# Revit family: Spot 1.0
name_source: partatom
category: Lighting Fixtures
revit_build: Autodesk Revit 2017 (Build: 20170419_0315(x64)
units: mm (PartAtom-declared; Revit-internal decimal feet)

## family parameters
Always vertical = No
Cut with Voids When Loaded = No
Light Source = No
OmniClass Number = 23.80.70.00
OmniClass Title = Lighting
Part Type = Normal
Room Calculation Point = No
Round Connector Dimension = Use Diameter
Shared = No
Work Plane-Based = No

## types (5) — shared parameters
Apparent Load Phase 1 = 2 W
Base = L&L_Steel inox AISI 316L
Base bracket = Spot 1.0_Base braket
Body = L&L_Steel inox AISI 316L
Bracket = L&L_Steel inox AISI 316L
CRI = ≥80
Code = -
Control system = -
Cutout dimensions = -
Delivered lumen output = 88 lm (3000K, 500mA, 20°)
Description = projector for outdoor applications (not suitable for use in swimming pools or fountains)
Energy efficiency class = A A+ A++
Features = -
Geometry = Spot 1.0_mod
H1 = 40 mm
Height mm = 55 mm
IP = IP68
LED Colour = 3000K (also available: 2700, 4000K, 5000K, Blue - ref. URL Technical sheet)
Length mm = 57 mm  [stored 0.187008 ft]
Lens = L&L_Tempered extra-clear glass
Lumen output at source = 145 lm (3000K, 500mA)
Manufacturer = L&L Luce&Light
Material = body and trim in AISI 316L stainless steel, screen in transparent, tempered glass
Model = Spot 1.0
Mounting = surface mounted (ceiling, wall, ground, spike, fastener strap)
No. and type of led = 1 power LED, 1/4 ANSI BIN, 50 000h L90 B10 (Ta 25°C)
Notes = version with elliptical optics available on request
Power = 2W
Power cables = includes 1,5 m neoprene cable, H05RN-F 2x0,35/0,75 Ø6,3 mm
Power supply = max 500mA
Power supply unit = not included
not included
not included
URL = https://www.lucelight.it
URL Accessories and power supply units = https://www.lucelight.it
URL Catalogue = https://www.lucelight.it
URL DXF = https://www.lucelight.it
URL Description = https://www.lucelight.it
URL General code = https://www.lucelight.it
URL IES Photometric file = https://www.lucelight.it
URL Image = https://www.lucelight.it
URL Technical sheet = https://www.lucelight.it
Vertical rotation max = 220.00°
Weight kg = 0.40 kg
Width mm = 30 mm  [stored 0.0984252 ft]
Wiring = series
X1 = 100 mm  [stored 0.328084 ft]

## per-type parameters (varying)
| type | Light Source | Optics |
| Spot 1.0 V 19° (3000K 1x500mA) | Light Source : V 19° | 19° |
| Spot 1.0 T 54° (3000K 1x500mA) | Light Source : T 54° | 54° |
| Spot 1.0 S 10° (3000K 1x500mA) | Light Source : S 10° | 10° |
| Spot 1.0 M 20° (3000K 1x500mA) | Light Source : M 20° | 20° |
| Spot 1.0 L 40° (3000K 1x500mA) | Light Source : L 40° | 40° |

note: [stored X ft] marks values corroborated as IEEE doubles in the binary element streams (Revit-internal decimal feet)

## geometry (parser evidence)
native form markers: Blend x2, Sweep x11
no freeform markers — native parametric forms only
